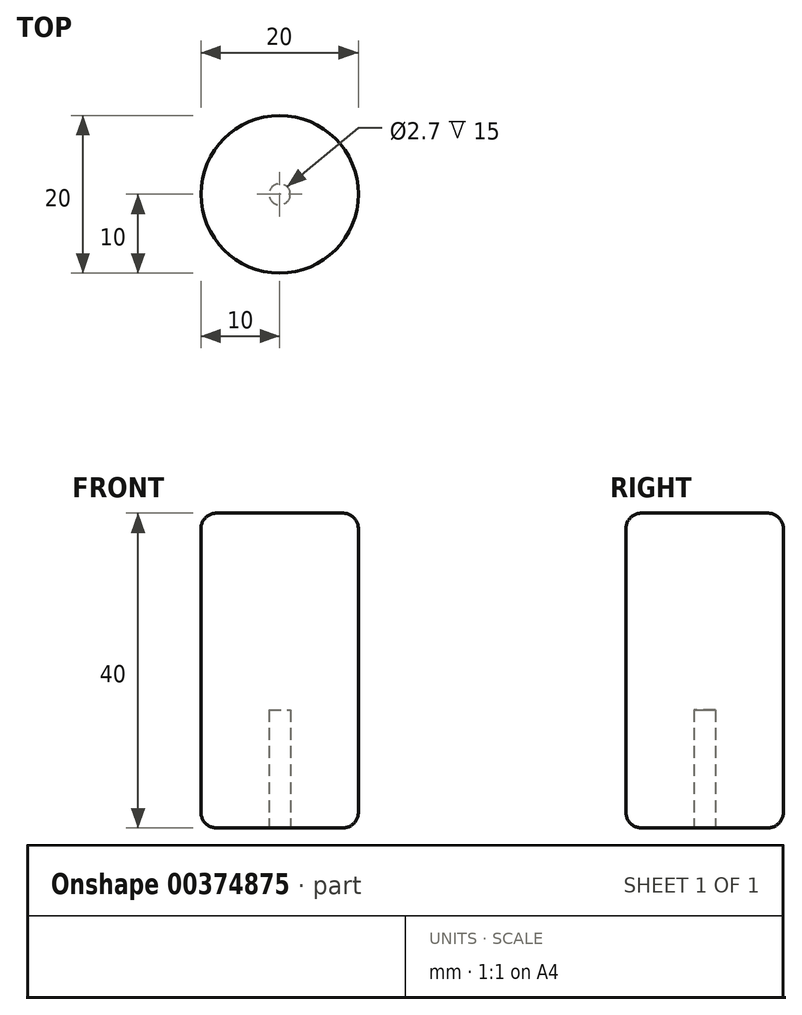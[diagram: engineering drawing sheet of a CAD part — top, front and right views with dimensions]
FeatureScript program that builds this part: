
annotation { "Feature Type Name" : "Feature", "Feature Type Description" : "" }
export const myFeature = defineFeature(function(context is Context, id is Id, definition is map)
    precondition{}
    {
        {
            var Q0;
            Q0=qCreatedBy(makeId("Front.planeOp"),FACE);
            var sketch = newSketch(context, id + "F0", { "sketchPlane" : qUnion([Q0])});
            skLineSegment(sketch, "E0", {"start": v(0, 0) * mm, "end": v(0, 13.05) * mm, "construction": true});
            skLineSegment(sketch, "E1.bottom", {"start": v(1.35, 0) * mm, "end": v(8, 0) * mm});
            skLineSegment(sketch, "E1.top", {"start": v(0, 40) * mm, "end": v(8, 40) * mm});
            skLineSegment(sketch, "E1.left", {"start": v(0, 15) * mm, "end": v(0, 40) * mm});
            skLineSegment(sketch, "E1.right", {"start": v(10, 2) * mm, "end": v(10, 38) * mm});
            skLineSegment(sketch, "E2", {"start": v(1.35, 0) * mm, "end": v(1.35, 15) * mm});
            skLineSegment(sketch, "E3", {"start": v(1.35, 15) * mm, "end": v(0, 15) * mm});
            skPoint(sketch, "E4.visualSharp", {"position": v(10, 40) * mm});
            skArc(sketch, "E4.filletArc", {"start": v(10, 38) * mm, "mid": v(9.41, 39.41) * mm, "end": v(8, 40) * mm});
            skPoint(sketch, "E5.visualSharp", {"position": v(10, 0) * mm});
            skArc(sketch, "E5.filletArc", {"start": v(8, 0) * mm, "mid": v(9.41, 0.59) * mm, "end": v(10, 2) * mm});
            skSolve(sketch);
        }
        {
            var Q0;
            Q0 = qSketchRegion(id + "F0", true);
            var Q1;
            Q1=sQuery(id+"F0.wireOp",EDGE,"E0");
            revolve(context, id + "F1", {"entities" : qUnion([Q0]), "axis" : qUnion([Q1]), "revolveType" : RevolveType.FULL});
        }
    });
